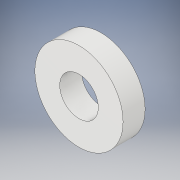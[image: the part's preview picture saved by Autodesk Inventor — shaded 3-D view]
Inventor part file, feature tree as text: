
AUTODESK INVENTOR PART (.ipt)
format: ipt  version: 2017 SP1 (Build 210196100, 196)  size: 107,008 bytes
history: native  units: in
note: dims shown in document units (in); Inventor stores cm internally (conversion verified against a paired STEP export)
features: extrude x1, sketch x1
ambient origin geometry x8: Origin, YZ Plane, XZ Plane, XY Plane, X Axis, Y Axis, Z Axis, Center Point
bodies: Solid1 (feature_tree)
feature tree (2):
  extrude  "Extrusion1"  Depth=0.0787in
  sketch  "Sketch1"  dims[d0=0.1378in d1=0.315in d2=0.0787in d3=0.0in]
